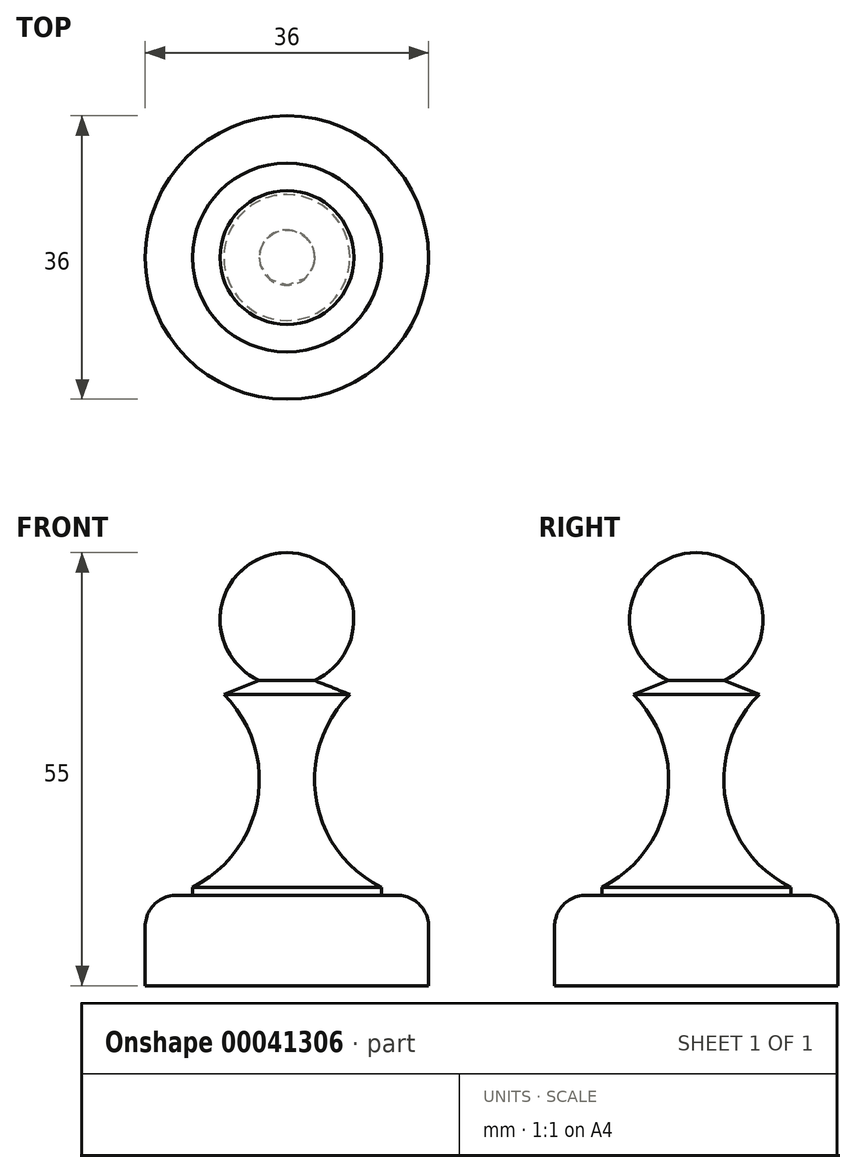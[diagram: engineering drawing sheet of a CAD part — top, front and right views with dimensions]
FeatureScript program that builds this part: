
annotation { "Feature Type Name" : "Feature", "Feature Type Description" : "" }
export const myFeature = defineFeature(function(context is Context, id is Id, definition is map)
    precondition{}
    {
        {
            var Q0;
            Q0=qCreatedBy(makeId("Front.planeOp"),FACE);
            var sketch = newSketch(context, id + "F0", { "sketchPlane" : qUnion([Q0])});
            skLineSegment(sketch, "E0", {"start": v(0, 0) * mm, "end": v(-18, 0) * mm});
            skPoint(sketch, "E1.visualSharp", {"position": v(-18, 0) * mm});
            skLineSegment(sketch, "E1.filletArc", {"start": v(-18, 0) * mm, "end": v(-18, 0) * mm});
            skLineSegment(sketch, "E2", {"start": v(-18, 0) * mm, "end": v(-18, 7.5) * mm});
            skLineSegment(sketch, "E3", {"start": v(-14, 11.5) * mm, "end": v(-12, 11.5) * mm});
            skLineSegment(sketch, "E4", {"start": v(-12, 11.5) * mm, "end": v(-12, 12.5) * mm});
            skPoint(sketch, "E5.visualSharp", {"position": v(-18, 11.5) * mm});
            skArc(sketch, "E5.filletArc", {"start": v(-14, 11.5) * mm, "mid": v(-16.83, 10.33) * mm, "end": v(-18, 7.5) * mm});
            skLineSegment(sketch, "E6", {"start": v(-8, 37) * mm, "end": v(-3.5, 38.76) * mm});
            skArc(sketch, "E7", {"start": v(0, 55) * mm, "mid": v(-8.3, 48.3) * mm, "end": v(-3.5, 38.76) * mm});
            skLineSegment(sketch, "E8", {"start": v(0, 55) * mm, "end": v(0, 0) * mm});
            skArc(sketch, "E9", {"start": v(-12, 12.5) * mm, "mid": v(-3.7, 23.72) * mm, "end": v(-8, 37) * mm});
            skSolve(sketch);
        }
        {
            var Q0;
            Q0=makeQuery(id+"F0.imprint","IMPRINT",FACE,{"disambiguationData":[TD([[makeQuery(id+"F0.imprint","IMPRINT",EDGE,{"derivedFrom":sQuery(id+"F0.wireOp",EDGE,"E0")}),-1.0]])]});
            var Q1;
            Q1=sQuery(id+"F0.wireOp",EDGE,"E8");
            revolve(context, id + "F1", {"entities" : qUnion([Q0]), "axis" : qUnion([Q1]), "revolveType" : RevolveType.FULL});
        }
    });
